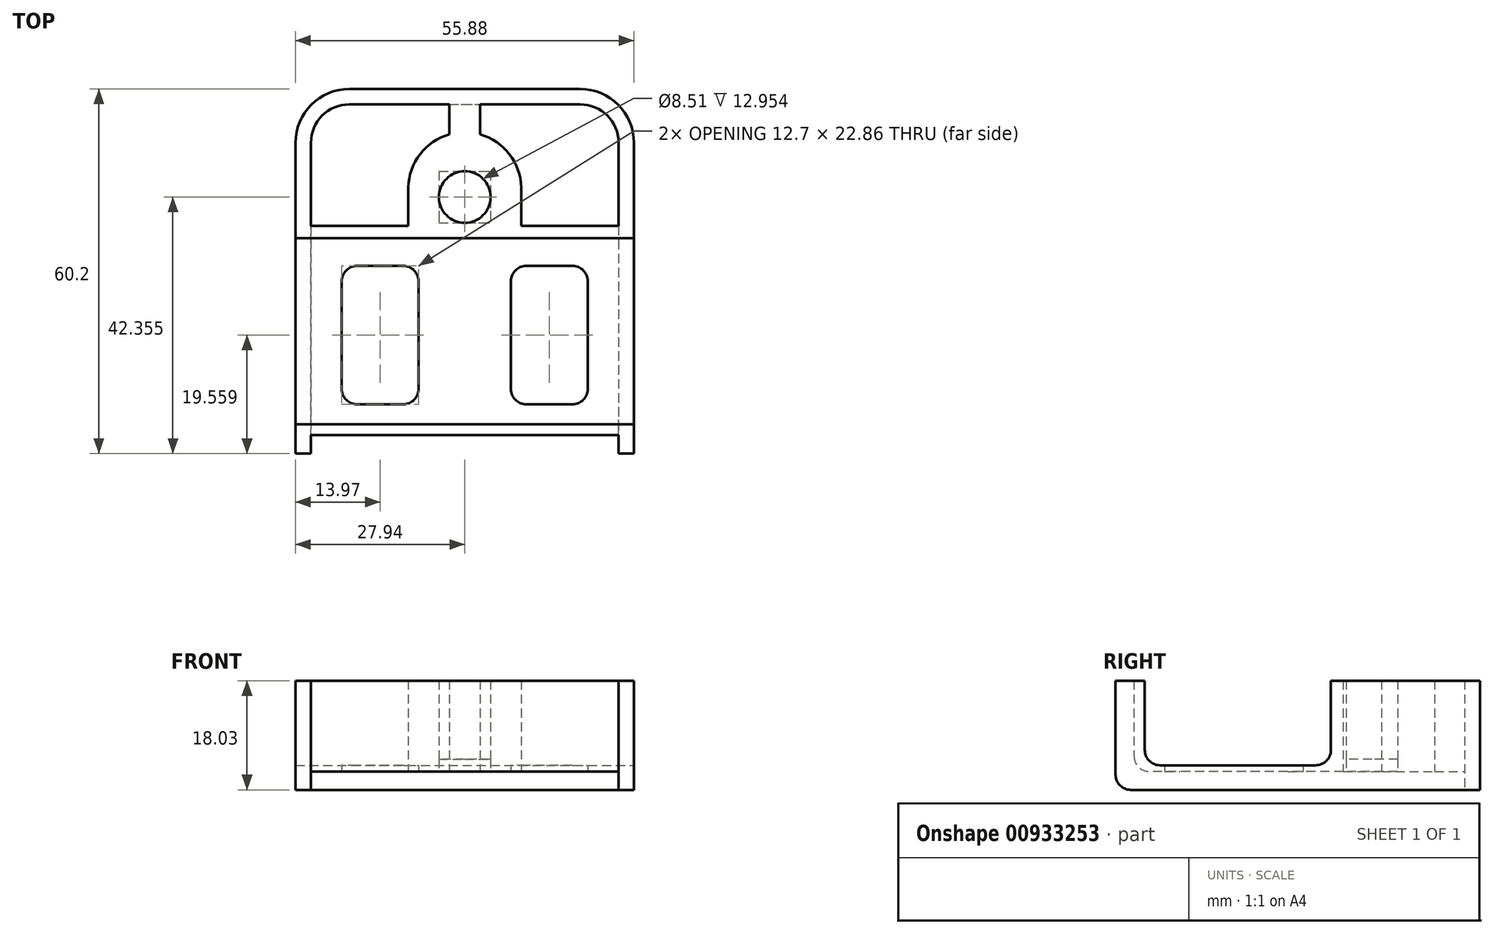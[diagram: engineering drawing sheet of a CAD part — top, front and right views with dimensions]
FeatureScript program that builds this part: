
annotation { "Feature Type Name" : "Feature", "Feature Type Description" : "" }
export const myFeature = defineFeature(function(context is Context, id is Id, definition is map)
    precondition{}
    {
        {
            var Q0;
            Q0=qCreatedBy(makeId("Top.planeOp"),FACE);
            var sketch = newSketch(context, id + "F0", { "sketchPlane" : qUnion([Q0])});
            skLineSegment(sketch, "E0.top", {"start": v(-27.94, -30.1) * mm, "end": v(-25.4, -30.1) * mm});
            skLineSegment(sketch, "E1", {"start": v(-25.4, -30.1) * mm, "end": v(-25.4, 21.2) * mm});
            skLineSegment(sketch, "E2", {"start": v(-19.05, 27.56) * mm, "end": v(19.05, 27.56) * mm});
            skLineSegment(sketch, "E3", {"start": v(25.4, 21.2) * mm, "end": v(25.4, -30.1) * mm});
            skPoint(sketch, "E4.visualSharp", {"position": v(-25.4, 27.56) * mm});
            skArc(sketch, "E4.filletArc", {"start": v(-19.05, 27.56) * mm, "mid": v(-23.54, 25.7) * mm, "end": v(-25.4, 21.2) * mm});
            skPoint(sketch, "E5.visualSharp", {"position": v(-27.94, 30.1) * mm});
            skPoint(sketch, "E6.visualSharp", {"position": v(25.4, 27.56) * mm});
            skArc(sketch, "E6.filletArc", {"start": v(25.4, 21.2) * mm, "mid": v(23.54, 25.7) * mm, "end": v(19.05, 27.56) * mm});
            skPoint(sketch, "E7.visualSharp", {"position": v(27.94, 30.1) * mm});
            skLineSegment(sketch, "E8.trimOffspring", {"start": v(25.4, -30.1) * mm, "end": v(27.94, -30.1) * mm});
            skLineSegment(sketch, "E9.0", {"start": v(27.94, 21.2) * mm, "end": v(27.94, -30.1) * mm});
            skLineSegment(sketch, "E9.1", {"start": v(-27.94, -30.1) * mm, "end": v(-27.94, 21.2) * mm});
            skArc(sketch, "E9.2", {"start": v(-19.05, 30.1) * mm, "mid": v(-25.34, 27.5) * mm, "end": v(-27.94, 21.2) * mm});
            skLineSegment(sketch, "E9.3", {"start": v(-19.05, 30.1) * mm, "end": v(19.05, 30.1) * mm});
            skArc(sketch, "E9.4", {"start": v(27.94, 21.2) * mm, "mid": v(25.34, 27.5) * mm, "end": v(19.05, 30.1) * mm});
            skSolve(sketch);
        }
        {
            var Q0;
            Q0 = qSketchRegion(id + "F0", true);
            extrude(context, id + "F1", {"entities" : qUnion([Q0]), "depth" : 18.03 * mm, "offsetDistance" : 25.4 * mm});
        }
        {
            var Q0;
            Q0=qCreatedBy(makeId("Top.planeOp"),FACE);
            cPlane(context, id + "F2", {"entities" : qUnion([Q0]), "cplaneType" : CPlaneType.OFFSET, "offset" : 3.05 * mm, "width" : 152.4 * mm, "height" : 152.4 * mm});
        }
        {
            var Q0;
            Q0=qCreatedBy(id+"F2.planeOp",FACE);
            var sketch = newSketch(context, id + "F3", { "sketchPlane" : qUnion([Q0])});
            skLineSegment(sketch, "E10", {"start": v(-25.4, -27.05) * mm, "end": v(25.4, -27.05) * mm});
            skLineSegment(sketch, "E11.bottom", {"start": v(-17.78, 0.89) * mm, "end": v(-10.16, 0.89) * mm});
            skLineSegment(sketch, "E11.top", {"start": v(-17.78, -21.97) * mm, "end": v(-10.16, -21.97) * mm});
            skLineSegment(sketch, "E11.left", {"start": v(-20.32, -1.65) * mm, "end": v(-20.32, -19.43) * mm});
            skLineSegment(sketch, "E11.right", {"start": v(-7.62, -1.65) * mm, "end": v(-7.62, -19.43) * mm});
            skLineSegment(sketch, "E12.bottom", {"start": v(10.16, 0.89) * mm, "end": v(17.78, 0.89) * mm});
            skLineSegment(sketch, "E12.top", {"start": v(10.16, -21.97) * mm, "end": v(17.78, -21.97) * mm});
            skLineSegment(sketch, "E12.left", {"start": v(7.62, -1.65) * mm, "end": v(7.62, -19.43) * mm});
            skLineSegment(sketch, "E12.right", {"start": v(20.32, -1.65) * mm, "end": v(20.32, -19.43) * mm});
            skLineSegment(sketch, "E13", {"start": v(-25.4, 7.5) * mm, "end": v(-25.4, -27.05) * mm});
            skLineSegment(sketch, "E14", {"start": v(25.4, 7.5) * mm, "end": v(25.4, -27.05) * mm});
            skPoint(sketch, "E15.visualSharp", {"position": v(-20.32, 0.89) * mm});
            skArc(sketch, "E15.filletArc", {"start": v(-17.78, 0.89) * mm, "mid": v(-19.58, 0.15) * mm, "end": v(-20.32, -1.65) * mm});
            skPoint(sketch, "E16.visualSharp", {"position": v(-7.62, 0.89) * mm});
            skArc(sketch, "E16.filletArc", {"start": v(-7.62, -1.65) * mm, "mid": v(-8.36, 0.15) * mm, "end": v(-10.16, 0.89) * mm});
            skPoint(sketch, "E17.visualSharp", {"position": v(-7.62, -21.97) * mm});
            skArc(sketch, "E17.filletArc", {"start": v(-10.16, -21.97) * mm, "mid": v(-8.36, -21.23) * mm, "end": v(-7.62, -19.43) * mm});
            skPoint(sketch, "E18.visualSharp", {"position": v(-20.32, -21.97) * mm});
            skArc(sketch, "E18.filletArc", {"start": v(-20.32, -19.43) * mm, "mid": v(-19.58, -21.23) * mm, "end": v(-17.78, -21.97) * mm});
            skPoint(sketch, "E19.visualSharp", {"position": v(7.62, 0.89) * mm});
            skArc(sketch, "E19.filletArc", {"start": v(10.16, 0.89) * mm, "mid": v(8.36, 0.15) * mm, "end": v(7.62, -1.65) * mm});
            skPoint(sketch, "E20.visualSharp", {"position": v(20.32, 0.89) * mm});
            skArc(sketch, "E20.filletArc", {"start": v(20.32, -1.65) * mm, "mid": v(19.58, 0.15) * mm, "end": v(17.78, 0.89) * mm});
            skPoint(sketch, "E21.visualSharp", {"position": v(20.32, -21.97) * mm});
            skArc(sketch, "E21.filletArc", {"start": v(17.78, -21.97) * mm, "mid": v(19.58, -21.23) * mm, "end": v(20.32, -19.43) * mm});
            skPoint(sketch, "E22.visualSharp", {"position": v(7.62, -21.97) * mm});
            skArc(sketch, "E22.filletArc", {"start": v(7.62, -19.43) * mm, "mid": v(8.36, -21.23) * mm, "end": v(10.16, -21.97) * mm});
            skLineSegment(sketch, "E23", {"start": v(-9.33, 7.5) * mm, "end": v(-9.33, 13.83) * mm});
            skLineSegment(sketch, "E24", {"start": v(9.33, 7.5) * mm, "end": v(9.33, 13.83) * mm});
            skArc(sketch, "E25", {"start": v(-9.33, 13.83) * mm, "mid": v(-7.38, 19.34) * mm, "end": v(-2.54, 22.6) * mm});
            skLineSegment(sketch, "E26.bottom", {"start": v(-4.25, 16.5) * mm, "end": v(4.25, 16.5) * mm});
            skLineSegment(sketch, "E26.top", {"start": v(-4.25, 8) * mm, "end": v(4.25, 8) * mm});
            skLineSegment(sketch, "E26.left", {"start": v(-4.25, 16.5) * mm, "end": v(-4.25, 8) * mm});
            skLineSegment(sketch, "E26.right", {"start": v(4.25, 16.5) * mm, "end": v(4.25, 8) * mm});
            skLineSegment(sketch, "E27", {"start": v(-2.54, 22.6) * mm, "end": v(-2.54, 27.56) * mm});
            skLineSegment(sketch, "E28", {"start": v(2.54, 22.6) * mm, "end": v(2.54, 27.56) * mm});
            skLineSegment(sketch, "E29", {"start": v(-2.54, 27.56) * mm, "end": v(2.54, 27.56) * mm});
            skArc(sketch, "E30.trimOffspring", {"start": v(2.54, 22.6) * mm, "mid": v(7.38, 19.34) * mm, "end": v(9.33, 13.83) * mm});
            skLineSegment(sketch, "E31", {"start": v(-25.4, 7.5) * mm, "end": v(-9.33, 7.5) * mm});
            skLineSegment(sketch, "E32.trimOffspring", {"start": v(9.33, 7.5) * mm, "end": v(25.4, 7.5) * mm});
            skSolve(sketch);
        }
        {
            var Q0;
            Q0 = qSketchRegion(id + "F3", true);
            extrude(context, id + "F4", {"entities" : qUnion([Q0]), "operationType" : NewBodyOperationType.ADD, "depth" : 2.03 * mm, "offsetDistance" : 25.4 * mm});
        }
        {
            var Q0;
            Q0=makeQuery(id+"F4.opExtrude","CAP_FACE",FACE,{"disambiguationData":[OSD([sQuery(id+"F3.wireOp",EDGE,"E10"),sQuery(id+"F3.wireOp",EDGE,"93U0UULe-PDUl-iimd-KyLi-UXtt8KRIJaTp"),sQuery(id+"F3.wireOp",EDGE,"E11.bottom"),sQuery(id+"F3.wireOp",EDGE,"E11.top"),sQuery(id+"F3.wireOp",EDGE,"E11.left"),sQuery(id+"F3.wireOp",EDGE,"E11.right"),sQuery(id+"F3.wireOp",EDGE,"E12.bottom"),sQuery(id+"F3.wireOp",EDGE,"E12.top"),sQuery(id+"F3.wireOp",EDGE,"E12.left"),sQuery(id+"F3.wireOp",EDGE,"E12.right"),sQuery(id+"F3.wireOp",EDGE,"E13"),sQuery(id+"F3.wireOp",EDGE,"E14"),sQuery(id+"F3.wireOp",EDGE,"E15.filletArc"),sQuery(id+"F3.wireOp",EDGE,"E16.filletArc"),sQuery(id+"F3.wireOp",EDGE,"E17.filletArc"),sQuery(id+"F3.wireOp",EDGE,"E18.filletArc"),sQuery(id+"F3.wireOp",EDGE,"E19.filletArc"),sQuery(id+"F3.wireOp",EDGE,"E20.filletArc"),sQuery(id+"F3.wireOp",EDGE,"E21.filletArc"),sQuery(id+"F3.wireOp",EDGE,"E22.filletArc"),sQuery(id+"F3.wireOp",EDGE,"E23"),sQuery(id+"F3.wireOp",EDGE,"E24"),sQuery(id+"F3.wireOp",EDGE,"E25"),sQuery(id+"F3.wireOp",EDGE,"E26.bottom"),sQuery(id+"F3.wireOp",EDGE,"E26.top"),sQuery(id+"F3.wireOp",EDGE,"E26.left"),sQuery(id+"F3.wireOp",EDGE,"E26.right"),sQuery(id+"F3.wireOp",EDGE,"E27"),sQuery(id+"F3.wireOp",EDGE,"E28"),sQuery(id+"F3.wireOp",EDGE,"E29"),sQuery(id+"F3.wireOp",EDGE,"E30.trimOffspring"),sQuery(id+"F3.wireOp",EDGE,"f5304f36-e2f0-4c72-b824-67432ffdbdb7.trimOffspring")])],"isStart":false});
            var sketch = newSketch(context, id + "F5", { "sketchPlane" : qUnion([Q0])});
            skLineSegment(sketch, "E33", {"start": v(-9.33, 7.5) * mm, "end": v(-9.33, 13.83) * mm});
            skLineSegment(sketch, "E34", {"start": v(9.33, 7.5) * mm, "end": v(9.33, 13.83) * mm});
            skCircle(sketch, "E35", {"center": v(0, 12.26) * mm, "radius": 4.25 * mm});
            skPoint(sketch, "E35.centerSnap0", {"position": v(0, 27.56) * mm});
            skArc(sketch, "E36", {"start": v(-9.33, 13.83) * mm, "mid": v(-7.38, 19.34) * mm, "end": v(-2.54, 22.6) * mm});
            skLineSegment(sketch, "E37", {"start": v(-2.54, 27.56) * mm, "end": v(-2.54, 22.6) * mm});
            skLineSegment(sketch, "E38", {"start": v(2.54, 27.56) * mm, "end": v(2.54, 22.6) * mm});
            skLineSegment(sketch, "E39", {"start": v(-2.54, 27.56) * mm, "end": v(2.54, 27.56) * mm});
            skArc(sketch, "E40.trimOffspring", {"start": v(2.54, 22.6) * mm, "mid": v(7.38, 19.34) * mm, "end": v(9.33, 13.83) * mm});
            skLineSegment(sketch, "E41", {"start": v(-9.33, 7.5) * mm, "end": v(-9.33, 7.5) * mm});
            skPoint(sketch, "E42.start.orphan", {"position": v(-25.4, 7.5) * mm});
            skLineSegment(sketch, "E43", {"start": v(-9.33, 7.5) * mm, "end": v(-25.4, 7.5) * mm});
            skLineSegment(sketch, "E44", {"start": v(-25.4, -27.05) * mm, "end": v(25.4, -27.05) * mm});
            skLineSegment(sketch, "E45", {"start": v(25.4, -27.05) * mm, "end": v(25.4, 7.5) * mm});
            skLineSegment(sketch, "E46", {"start": v(25.4, 7.5) * mm, "end": v(9.33, 7.5) * mm});
            skLineSegment(sketch, "E47", {"start": v(-25.4, 7.5) * mm, "end": v(-25.4, -27.05) * mm});
            skSolve(sketch);
        }
        {
            var Q0;
            Q0 = qSketchRegion(id + "F5", true);
            var Q1;
            Q1=makeQuery(id+"F1.opExtrude","CAP_FACE",FACE,{"disambiguationData":[OSD([sQuery(id+"F0.wireOp",EDGE,"E0.top"),sQuery(id+"F0.wireOp",EDGE,"E1"),sQuery(id+"F0.wireOp",EDGE,"E2"),sQuery(id+"F0.wireOp",EDGE,"E3"),sQuery(id+"F0.wireOp",EDGE,"E4.filletArc"),sQuery(id+"F0.wireOp",EDGE,"E6.filletArc"),sQuery(id+"F0.wireOp",EDGE,"E8.trimOffspring"),sQuery(id+"F0.wireOp",EDGE,"E9.0"),sQuery(id+"F0.wireOp",EDGE,"E9.1"),sQuery(id+"F0.wireOp",EDGE,"E9.2"),sQuery(id+"F0.wireOp",EDGE,"E9.3"),sQuery(id+"F0.wireOp",EDGE,"E9.4")])],"isStart":false});
            extrude(context, id + "F6", {"entities" : qUnion([Q0]), "operationType" : NewBodyOperationType.ADD, "endBound" : BoundingType.UP_TO_SURFACE, "depth" : 25.4 * mm, "endBoundEntityFace" : qUnion([Q1]), "offsetDistance" : 25.4 * mm});
        }
        {
            var Q0;
            Q0=makeQuery(id+"F1.opExtrude","SWEPT_FACE",FACE,{"disambiguationData":[OSD([sQuery(id+"F0.wireOp",EDGE,"E9.0")])]});
            var sketch = newSketch(context, id + "F7", { "sketchPlane" : qUnion([Q0])});
            skLineSegment(sketch, "E48", {"start": v(-25.27, 18.03) * mm, "end": v(-25.27, 6.6) * mm});
            skLineSegment(sketch, "E49", {"start": v(-22.73, 4.06) * mm, "end": v(2.92, 4.06) * mm});
            skLineSegment(sketch, "E50", {"start": v(5.46, 6.6) * mm, "end": v(5.46, 18.03) * mm});
            skLineSegment(sketch, "E51", {"start": v(5.46, 18.03) * mm, "end": v(-25.27, 18.03) * mm});
            skPoint(sketch, "E52.visualSharp", {"position": v(-25.27, 4.06) * mm});
            skArc(sketch, "E52.filletArc", {"start": v(-25.27, 6.6) * mm, "mid": v(-24.53, 4.8) * mm, "end": v(-22.73, 4.06) * mm});
            skPoint(sketch, "E53.visualSharp", {"position": v(5.46, 4.06) * mm});
            skArc(sketch, "E53.filletArc", {"start": v(2.92, 4.06) * mm, "mid": v(4.72, 4.8) * mm, "end": v(5.46, 6.6) * mm});
            skSolve(sketch);
        }
        {
            var Q0;
            Q0 = qSketchRegion(id + "F7", true);
            extrude(context, id + "F8", {"entities" : qUnion([Q0]), "operationType" : NewBodyOperationType.REMOVE, "endBound" : BoundingType.THROUGH_ALL, "oppositeDirection" : true, "depth" : 25.4 * mm, "offsetDistance" : 25.4 * mm});
        }
        {
            var Q0;
            Q0=makeQuery(id+"F1.opExtrude","CAP_EDGE",EDGE,{"disambiguationData":[OSD([sQuery(id+"F0.wireOp",EDGE,"E0.top")])],"isStart":true});
            var Q1;
            Q1=makeQuery(id+"F1.opExtrude","CAP_EDGE",EDGE,{"disambiguationData":[OSD([sQuery(id+"F0.wireOp",EDGE,"E8.trimOffspring")])],"isStart":true});
            var Q2;
            Q2=makeQuery(id+"F4.opExtrude","CAP_EDGE",EDGE,{"disambiguationData":[OSD([sQuery(id+"F3.wireOp",EDGE,"E10")])],"isStart":true});
            fillet(context, id + "F9", {"entities" : qUnion([Q0, Q1, Q2]), "radius" : 2.54 * mm, "tangentPropagation" : true, "allowEdgeOverflow" : false});
        }
    });
